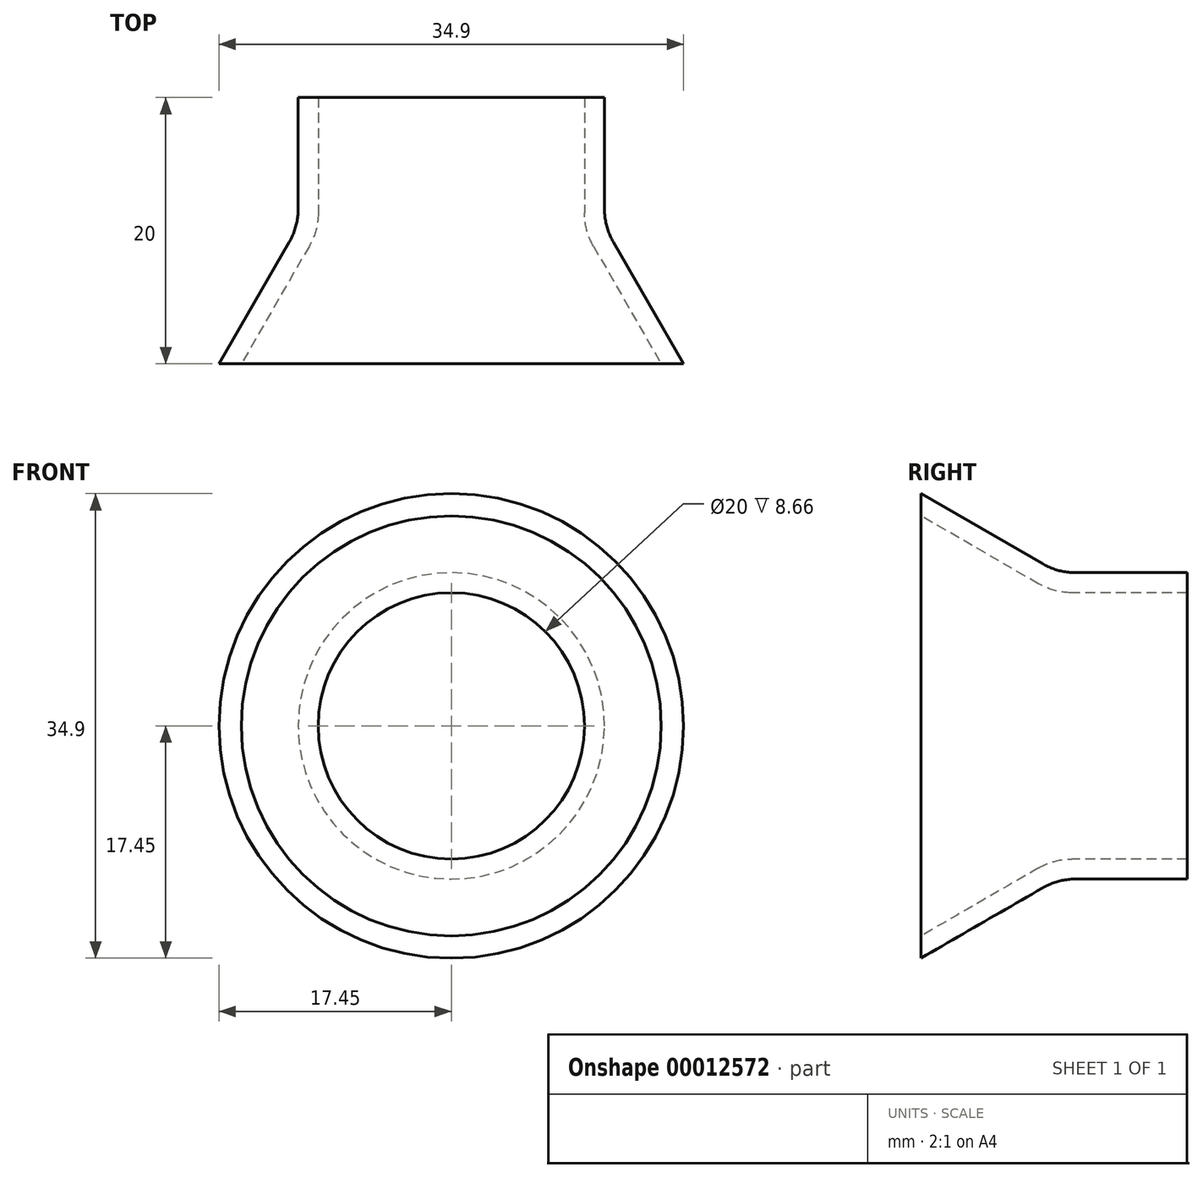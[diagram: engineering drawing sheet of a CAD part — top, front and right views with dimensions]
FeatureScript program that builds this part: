
annotation { "Feature Type Name" : "Feature", "Feature Type Description" : "" }
export const myFeature = defineFeature(function(context is Context, id is Id, definition is map)
    precondition{}
    {
        {
            var Q0;
            Q0=qCreatedBy(makeId("Right.planeOp"),FACE);
            var sketch = newSketch(context, id + "F0", { "sketchPlane" : qUnion([Q0])});
            skLineSegment(sketch, "E0", {"start": v(0, 0) * mm, "end": v(6.48, 0) * mm, "construction": true});
            skLineSegment(sketch, "E1", {"start": v(0, 10) * mm, "end": v(10, 10) * mm});
            skLineSegment(sketch, "E2", {"start": v(10, 10) * mm, "end": v(10, 11.5) * mm});
            skLineSegment(sketch, "E3", {"start": v(10, 11.5) * mm, "end": v(0.3, 11.5) * mm});
            skLineSegment(sketch, "E4", {"start": v(0.3, 11.5) * mm, "end": v(-10, 17.45) * mm});
            skLineSegment(sketch, "E5", {"start": v(-10, 17.45) * mm, "end": v(-10, 15.77) * mm});
            skLineSegment(sketch, "E6", {"start": v(-10, 15.77) * mm, "end": v(0, 10) * mm});
            skLineSegment(sketch, "E7", {"start": v(0.3, 11.5) * mm, "end": v(-0.09, 10.05) * mm, "construction": true});
            skPoint(sketch, "E8", {"position": v(10, -10) * mm});
            skSolve(sketch);
        }
        {
            var Q0;
            Q0 = qSketchRegion(id + "F0", true);
            var Q1;
            Q1=sQuery(id+"F0.wireOp",EDGE,"E0");
            revolve(context, id + "F1", {"entities" : qUnion([Q0]), "axis" : qUnion([Q1]), "revolveType" : RevolveType.FULL});
        }
        {
            var Q0;
            Q0=makeQuery(id+"F1.opRevolve","SWEPT_EDGE",EDGE,{"disambiguationData":[OSD([sQuery(id+"F0.wireOp",EDGE,"E3"),sQuery(id+"F0.wireOp",EDGE,"E4")])]});
            var Q1;
            Q1=makeQuery(id+"F1.opRevolve","SWEPT_EDGE",EDGE,{"disambiguationData":[OSD([sQuery(id+"F0.wireOp",EDGE,"E1"),sQuery(id+"F0.wireOp",EDGE,"E6")])]});
            fillet(context, id + "F2", {"entities" : qUnion([Q0, Q1]), "radius" : 5 * mm, "tangentPropagation" : true, "allowEdgeOverflow" : false});
        }
    });
